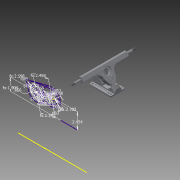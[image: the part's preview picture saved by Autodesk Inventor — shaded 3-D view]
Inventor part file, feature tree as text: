
AUTODESK INVENTOR PART (.ipt)
format: ipt  version: 2014 SP1 (Build 180222100, 222)  size: 492,032 bytes
history: native  units: in
note: dims shown in document units (in); Inventor stores cm internally (conversion verified against a paired STEP export)
features: other x10, sketch x1
ambient origin geometry x8: Origin, YZ Plane, XZ Plane, XY Plane, X Axis, Y Axis, Z Axis, Center Point
bodies: Solid1 (feature_tree)
feature tree (11):
  other  "truck.iam"
  other  "baseplate.ipt:1"
  other  "hanger.ipt:1"
  sketch  "Sketch1"  dims[d0=0.3937in d2=0.8661in d3=0.1693in d5=0.8661in d6=2.5984in d7=2.4577in d13=1.5748in d15=360.0deg d17=2.454in d18=1.9042in d31=2.3827in d32=0.1693in d33=0.8661in d34=0.5in d35=2.5327in d36=0.1693in d37=0.8661in d38=0.5in d39=1.5748in d41=360.0deg d43=1.5748in d45=360.0deg d52=0.0in d53=2.7031in d58=0.5in d59=0.5in d60=0.05in d61=0.05in d62=0.74in d63=0.355in d64=0.205in d65=0.1915in d66=0.355in d67=0.2in]
  other  "Work Axis1"
  other  "Work Axis2"
  other  "Work Axis3"
  other  "Work Axis1_1"
  other  "Work Axis2_1"
  other  "Work Axis3_1"
  other  "Work Point1"
